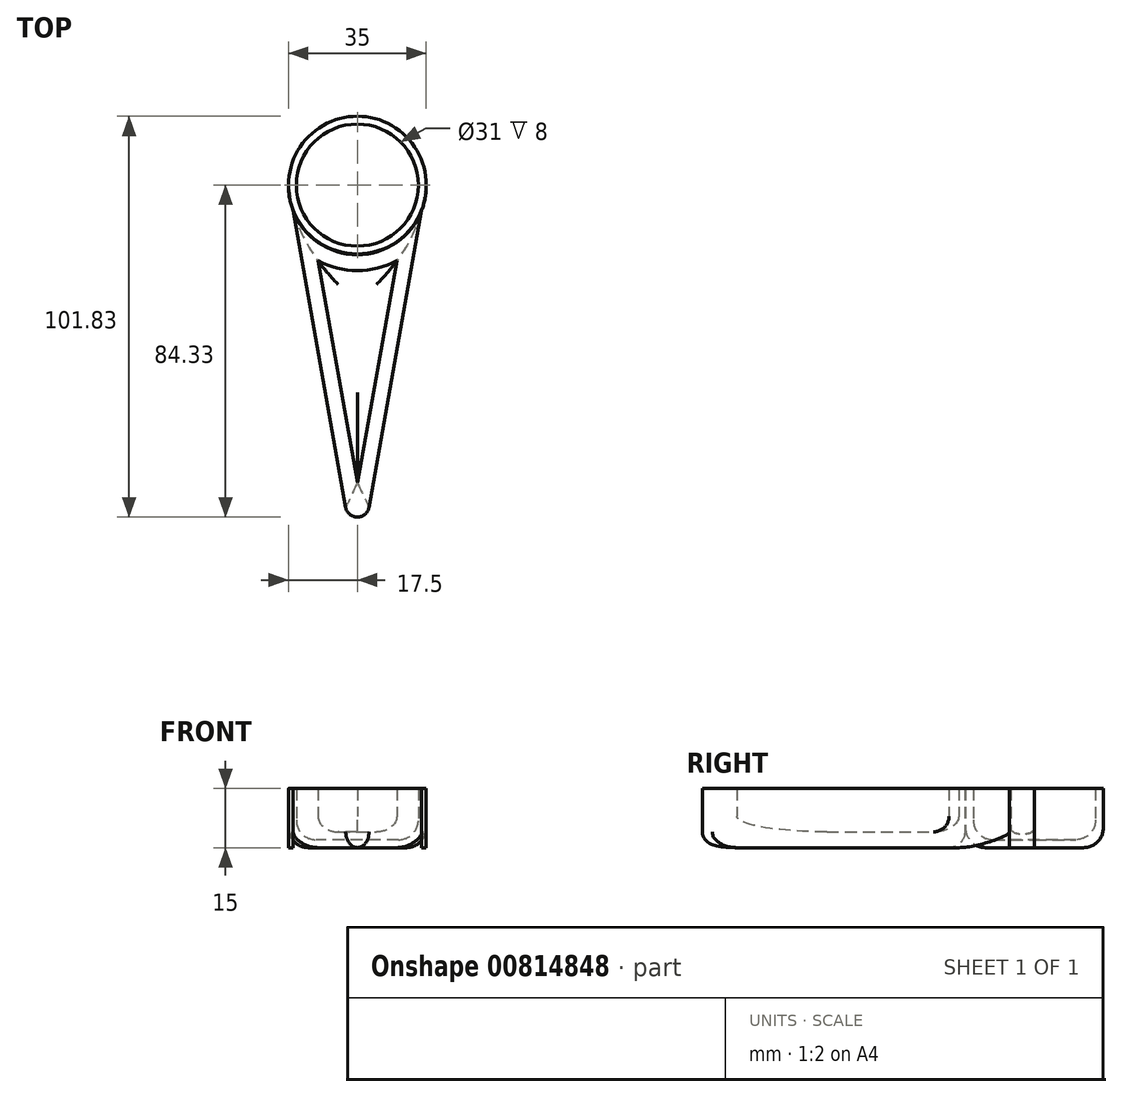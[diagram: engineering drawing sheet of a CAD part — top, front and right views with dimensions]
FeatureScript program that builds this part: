
annotation { "Feature Type Name" : "Feature", "Feature Type Description" : "" }
export const myFeature = defineFeature(function(context is Context, id is Id, definition is map)
    precondition{}
    {
        {
            var Q0;
            Q0=qCreatedBy(makeId("Top.planeOp"),FACE);
            var sketch = newSketch(context, id + "F0", { "sketchPlane" : qUnion([Q0])});
            skCircle(sketch, "E0", {"center": v(0, 0) * mm, "radius": 17.5 * mm});
            skSolve(sketch);
        }
        {
            var Q0;
            Q0 = qSketchRegion(id + "F0", true);
            extrude(context, id + "F1", {"entities" : qUnion([Q0]), "depth" : 15 * mm, "offsetDistance" : 25 * mm});
        }
        {
            var Q0;
            Q0=makeQuery(id+"F1.opExtrude","CAP_FACE",FACE,{"disambiguationData":[OSD([sQuery(id+"F0.wireOp",EDGE,"E0")])],"isStart":false});
            shell(context, id + "F2", {"entities" : qUnion([Q0]), "thickness" : 2 * mm});
        }
        {
            var Q0;
            Q0=makeQuery(id+"F1.opExtrude","CAP_FACE",FACE,{"disambiguationData":[OSD([sQuery(id+"F0.wireOp",EDGE,"E0")])],"isStart":true});
            fillet(context, id + "F3", {"entities" : qUnion([Q0]), "radius" : 5 * mm, "tangentPropagation" : true, "allowEdgeOverflow" : false});
        }
        {
            var Q0;
            {var subQ0=sQuery(id+"F0.wireOp",EDGE,"E0");Q0=makeQuery(id+"F2.opShell","OFFSET_FACE",FACE,{"disambiguationData":[OSD([subQ0]),TDD([makeQuery(id+"F1.opExtrude","CAP_FACE",FACE,{"disambiguationData":[OSD([subQ0])],"isStart":true})])]});}
            fillet(context, id + "F4", {"entities" : qUnion([Q0]), "radius" : 5 * mm, "tangentPropagation" : true, "allowEdgeOverflow" : false});
        }
        {
            var Q0;
            Q0=qCreatedBy(makeId("Top.planeOp"),FACE);
            var sketch = newSketch(context, id + "F5", { "sketchPlane" : qUnion([Q0])});
            skLineSegment(sketch, "E1", {"start": v(-17.5, 0) * mm, "end": v(0, -98.47) * mm});
            skLineSegment(sketch, "E2", {"start": v(0, -98.47) * mm, "end": v(17.5, 0) * mm});
            skArc(sketch, "E3", {"start": v(-17.5, 0) * mm, "mid": v(0, -17.7) * mm, "end": v(17.5, 0) * mm});
            skSolve(sketch);
        }
        {
            var Q0;
            Q0 = qSketchRegion(id + "F5", true);
            extrude(context, id + "F6", {"entities" : qUnion([Q0]), "operationType" : NewBodyOperationType.ADD, "depth" : 15 * mm, "offsetDistance" : 25 * mm});
        }
        {
            var Q0;
            {var subQ0=sQuery(id+"F5.wireOp",EDGE,"E3");Q0=makeQuery(id+"F6.opExtrude","SWEPT_FACE",FACE,{"disambiguationData":[OSD([subQ0]),TDD([makeQuery(id+"F5.imprint","IMPRINT",EDGE,{"disambiguationData":[TD([[makeQuery(id+"F5.imprint","INTERSECT",VERTEX,{"disambiguationData":[OD(1.0)],"derivedFrom":[sQuery(id+"F5.wireOp",EDGE,"E1"),subQ0]}),-1.0]])],"derivedFrom":subQ0})])]});}
            var Q1;
            {var subQ0=sQuery(id+"F5.wireOp",EDGE,"E3");var subQ1=sQuery(id+"F5.wireOp",EDGE,"E1");Q1=makeQuery(id+"F6.opExtrude","CAP_EDGE",EDGE,{"disambiguationData":[OSD([subQ0]),TDD([makeQuery(id+"F5.imprint","IMPRINT",EDGE,{"disambiguationData":[TD([[makeQuery(id+"F5.imprint","INTERSECT",VERTEX,{"disambiguationData":[OD(0.0)],"derivedFrom":[subQ1,subQ0]}),-1.0]])],"derivedFrom":subQ0})])],"isStart":true});}
            var Q2;
            {var subQ0=sQuery(id+"F5.wireOp",EDGE,"E3");var subQ1=sQuery(id+"F5.wireOp",EDGE,"E2");Q2=makeQuery(id+"F6.opExtrude","CAP_EDGE",EDGE,{"disambiguationData":[OSD([subQ1]),TDD([makeQuery(id+"F5.imprint","IMPRINT",EDGE,{"disambiguationData":[TD([[makeQuery(id+"F5.imprint","INTERSECT",VERTEX,{"disambiguationData":[OD(0.0)],"derivedFrom":[subQ1,subQ0]}),1.0]])],"derivedFrom":subQ1})])],"isStart":true});}
            var Q3;
            Q3=makeQuery(id+"F6.opExtrude","CAP_FACE",FACE,{"disambiguationData":[OSD([sQuery(id+"F5.wireOp",EDGE,"E1"),sQuery(id+"F5.wireOp",EDGE,"E2"),sQuery(id+"F5.wireOp",EDGE,"E3")])],"isStart":true});
            fillet(context, id + "F7", {"entities" : qUnion([Q0, Q1, Q2, Q3]), "radius" : 4 * mm, "tangentPropagation" : true, "allowEdgeOverflow" : false});
        }
        {
            var Q0;
            Q0=makeQuery(id+"F6.opExtrude","CAP_FACE",FACE,{"disambiguationData":[OSD([sQuery(id+"F5.wireOp",EDGE,"E1"),sQuery(id+"F5.wireOp",EDGE,"E2"),sQuery(id+"F5.wireOp",EDGE,"E3")])],"isStart":false});
            shell(context, id + "F8", {"entities" : qUnion([Q0]), "thickness" : 4 * mm});
        }
        {
            var Q0;
            Q0=makeQuery(id+"F8.opShell","OFFSET_FACE",FACE,{"disambiguationData":[OSD([sQuery(id+"F5.wireOp",EDGE,"E1"),sQuery(id+"F5.wireOp",EDGE,"E2"),sQuery(id+"F5.wireOp",EDGE,"E3")])]});
            fillet(context, id + "F9", {"entities" : qUnion([Q0]), "radius" : 4 * mm, "tangentPropagation" : true, "allowEdgeOverflow" : false});
        }
        {
            var Q0;
            Q0=makeQuery(id+"F6.opExtrude","SWEPT_EDGE",EDGE,{"disambiguationData":[OSD([sQuery(id+"F5.wireOp",EDGE,"E1"),sQuery(id+"F5.wireOp",EDGE,"E2")])]});
            fillet(context, id + "F10", {"entities" : qUnion([Q0]), "radius" : 3 * mm, "tangentPropagation" : true, "allowEdgeOverflow" : false});
        }
    });
